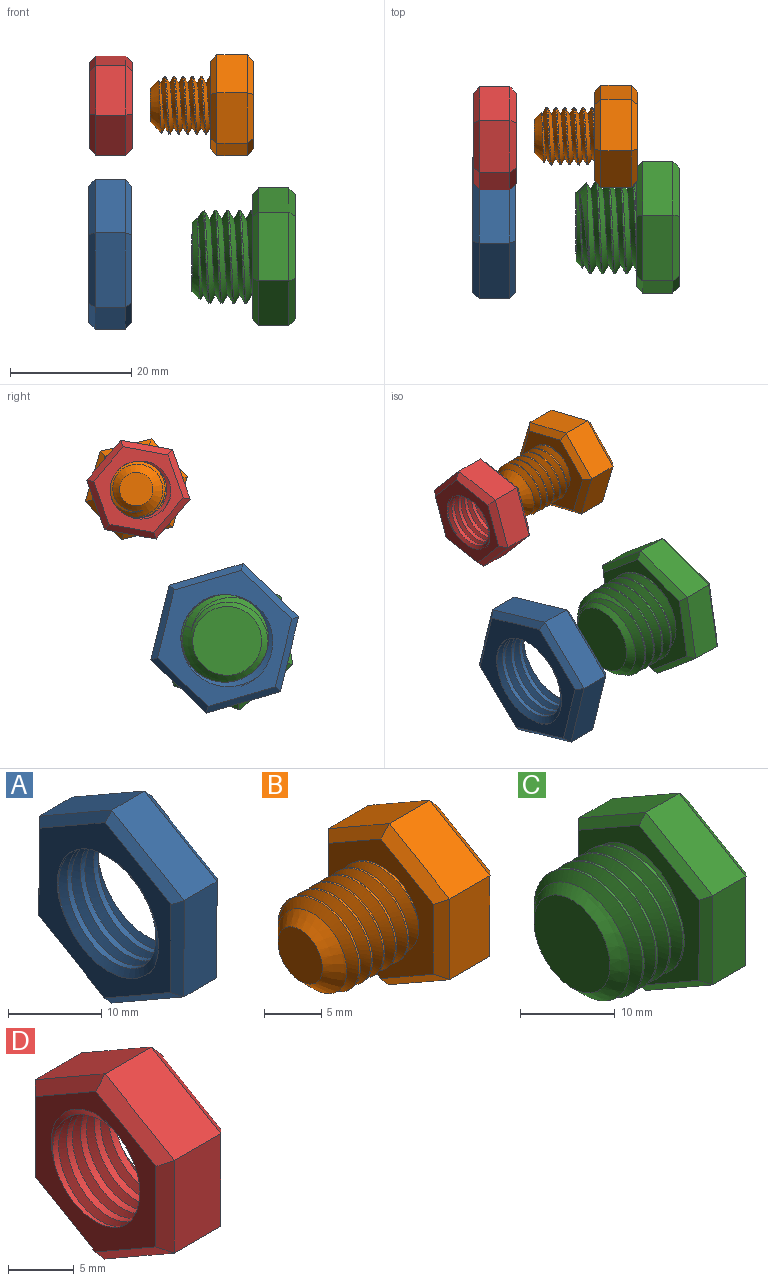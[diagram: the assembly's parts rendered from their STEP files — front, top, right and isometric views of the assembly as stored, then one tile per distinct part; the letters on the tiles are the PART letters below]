
ASSEMBLY  parts=4 mates=2
PART A: 23 faces, bbox 9.3x22.7x26 mm
  f0: cylinder r=7.24mm len=14.48mm, axis (1,0,0), area 111.6mm2, adj f7,f8,f21,f22
  f1: plane 10.98x6.38mm, normal (0,-0.5,0.86), area 63.5mm2, adj f2,f6,f14,f18
  f2: plane 12.7x5mm, normal (0,-1,0), area 63.5mm2, adj f1,f3,f12,f16
  f3: plane 11.02x6.32mm, normal (0,-0.5,-0.87), area 63.5mm2, adj f2,f4,f10,f15
  f4: plane 10.98x6.38mm, normal (0,0.5,-0.86), area 63.5mm2, adj f3,f5,f9,f17
  f5: plane 12.7x5mm, normal (0,1,0), area 63.5mm2, adj f4,f6,f11,f19
  f6: plane 11.02x6.32mm, normal (0,0.5,0.87), area 63.5mm2, adj f1,f5,f13,f20
  f7: plane 23.73x20.67mm, normal (-1,0,0), area 164.4mm2, adj f0,f9,f10,f11,f12,f13,f14,f21
  f8: plane 23.73x20.67mm, normal (1,0,0), area 164.4mm2, adj f0,f15,f16,f17,f18,f19,f20,f21
  f9: plane 10.99x6.96mm, normal (-0.71,0.36,-0.61), area 17.1mm2, adj f4,f7,f10,f11
  f10: plane 11.02x6.9mm, normal (-0.71,-0.35,-0.61), area 17.1mm2, adj f3,f7,f9,f12
  f11: plane 12.7x1.03mm, normal (-0.71,0.71,0), area 17.1mm2, adj f5,f7,f9,f13
  f12: plane 12.7x1.03mm, normal (-0.71,-0.71,0), area 17.1mm2, adj f2,f7,f10,f14
  f13: plane 11.02x6.9mm, normal (-0.71,0.35,0.61), area 17.1mm2, adj f6,f7,f11,f14
  f14: plane 10.99x6.96mm, normal (-0.71,-0.36,0.61), area 17.1mm2, adj f1,f7,f12,f13
  f15: plane 11.02x6.9mm, normal (0.71,-0.35,-0.61), area 17.1mm2, adj f3,f8,f16,f17
  f16: plane 12.7x1.03mm, normal (0.71,-0.71,0), area 17.1mm2, adj f2,f8,f15,f18
  f17: plane 10.99x6.96mm, normal (0.71,0.36,-0.61), area 17.1mm2, adj f4,f8,f15,f19
  f18: plane 10.99x6.96mm, normal (0.71,-0.36,0.61), area 17.1mm2, adj f1,f8,f16,f20
  f19: plane 12.7x1.03mm, normal (0.71,0.71,0), area 17.1mm2, adj f5,f8,f17,f20
  f20: plane 11.02x6.9mm, normal (0.71,0.35,0.61), area 17.1mm2, adj f6,f8,f18,f19
  f21: bspline ~19.31x16.73mm, area 223mm2, adj f0,f7,f8,f22
  f22: bspline ~19.31x16.73mm, area 223mm2, adj f0,f7,f8,f21
PART B: 25 faces, bbox 17.8x15.9x18.1 mm
  f0: cylinder r=4.75mm len=9.5mm, axis (1,0,0), area 28.1mm2, adj f1,f2,f4,f12
  f1: bspline ~10.97x9.91mm, area 196.7mm2, adj f0,f2,f4,f12
  f2: bspline ~10.97x10.66mm, area 196.6mm2, adj f0,f1,f4,f12
  f3: plane 5.5x5.5mm, normal (-1,0,0), area 23.8mm2, adj f4
  f4: cone r=4.75mm half-angle=45deg, axis (1,0,0), area 47.4mm2, adj f0,f1,f2,f3
  f5: plane 7.48x5mm, normal (0,-0.5,0.86), area 43.3mm2, adj f6,f10,f18,f22
  f6: plane 8.66x5mm, normal (0,-1,0), area 43.3mm2, adj f5,f7,f16,f20
  f7: plane 7.52x5mm, normal (0,-0.5,-0.87), area 43.3mm2, adj f6,f8,f14,f19
  f8: plane 7.48x5mm, normal (0,0.5,-0.86), area 43.3mm2, adj f7,f9,f13,f21
  f9: plane 8.66x5mm, normal (0,1,0), area 43.3mm2, adj f8,f10,f15,f23
  f10: plane 7.52x5mm, normal (0,0.5,0.87), area 43.3mm2, adj f5,f9,f17,f24
  f11: plane 15.01x13.03mm, normal (1,0,0), area 146.4mm2, adj f13,f14,f15,f16,f17,f18
  f12: plane 15.83x13.85mm, normal (-1,0,0), area 89.2mm2, adj f0,f1,f2,f19,f20,f21,f22,f23
  f13: plane 7.49x4.93mm, normal (0.71,0.36,-0.61), area 11.4mm2, adj f8,f11,f14,f15
  f14: plane 7.52x4.88mm, normal (0.71,-0.35,-0.61), area 11.4mm2, adj f7,f11,f13,f16
  f15: plane 8.66x1.03mm, normal (0.71,0.71,0), area 11.4mm2, adj f9,f11,f13,f17
  f16: plane 8.66x1.03mm, normal (0.71,-0.71,0), area 11.4mm2, adj f6,f11,f14,f18
  f17: plane 7.52x4.88mm, normal (0.71,0.35,0.61), area 11.4mm2, adj f10,f11,f15,f18
  f18: plane 7.49x4.93mm, normal (0.71,-0.36,0.61), area 11.4mm2, adj f5,f11,f16,f17
  f19: plane 7.52x4.88mm, normal (-0.71,-0.35,-0.61), area 11.4mm2, adj f7,f12,f20,f21
  f20: plane 8.66x1.03mm, normal (-0.71,-0.71,0), area 11.4mm2, adj f6,f12,f19,f22
  f21: plane 7.49x4.93mm, normal (-0.71,0.36,-0.61), area 11.4mm2, adj f8,f12,f19,f23
  f22: plane 7.49x4.93mm, normal (-0.71,-0.36,0.61), area 11.4mm2, adj f5,f12,f20,f24
  f23: plane 8.66x1.03mm, normal (-0.71,0.71,0), area 11.4mm2, adj f9,f12,f21,f24
  f24: plane 7.52x4.88mm, normal (-0.71,0.35,0.61), area 11.4mm2, adj f10,f12,f22,f23
PART C: 26 faces, bbox 17.7x20x23.1 mm
  f0: cylinder r=7.68mm len=15.36mm, axis (1,0,0), area 49.5mm2, adj f1,f2,f5,f13
  f1: bspline ~17.74x15.36mm, area 332.4mm2, adj f0,f2,f4,f5,f13
  f2: bspline ~17.74x15.36mm, area 332.4mm2, adj f0,f1,f4,f5,f13
  f3: plane 11.36x11.36mm, normal (-1,0,0), area 101.4mm2, adj f4
  f4: cone r=7.68mm half-angle=45deg, axis (1,0,0), area 63.2mm2, adj f1,f2,f3,f5
  f5: cone r=7.68mm half-angle=45deg, axis (1,0,0), area 13.2mm2, adj f0,f1,f2,f4
  f6: plane 9.98x5.81mm, normal (0,-0.5,0.86), area 57.7mm2, adj f7,f11,f19,f23
  f7: plane 11.55x5mm, normal (0,-1,0), area 57.7mm2, adj f6,f8,f17,f21
  f8: plane 10.02x5.74mm, normal (0,-0.5,-0.87), area 57.7mm2, adj f7,f9,f15,f20
  f9: plane 9.98x5.81mm, normal (0,0.5,-0.86), area 57.7mm2, adj f8,f10,f14,f22
  f10: plane 11.55x5mm, normal (0,1,0), area 57.7mm2, adj f9,f11,f16,f24
  f11: plane 10.02x5.74mm, normal (0,0.5,0.87), area 57.7mm2, adj f6,f10,f18,f25
  f12: plane 20.78x18.04mm, normal (1,0,0), area 280.6mm2, adj f14,f15,f16,f17,f18,f19
  f13: plane 20.78x18.04mm, normal (-1,0,0), area 125.2mm2, adj f0,f1,f2,f20,f21,f22,f23,f24
  f14: plane 9.98x6.38mm, normal (0.71,0.36,-0.61), area 15.5mm2, adj f9,f12,f15,f16
  f15: plane 10.02x6.32mm, normal (0.71,-0.35,-0.61), area 15.5mm2, adj f8,f12,f14,f17
  f16: plane 11.55x1.04mm, normal (0.71,0.71,0), area 15.5mm2, adj f10,f12,f14,f18
  f17: plane 11.55x1.04mm, normal (0.71,-0.71,0), area 15.5mm2, adj f7,f12,f15,f19
  f18: plane 10.02x6.32mm, normal (0.71,0.35,0.61), area 15.5mm2, adj f11,f12,f16,f19
  f19: plane 9.98x6.38mm, normal (0.71,-0.36,0.61), area 15.5mm2, adj f6,f12,f17,f18
  f20: plane 10.02x6.32mm, normal (-0.71,-0.35,-0.61), area 15.5mm2, adj f8,f13,f21,f22
  f21: plane 11.55x1.04mm, normal (-0.71,-0.71,0), area 15.5mm2, adj f7,f13,f20,f23
  f22: plane 9.98x6.38mm, normal (-0.71,0.36,-0.61), area 15.5mm2, adj f9,f13,f20,f24
  f23: plane 9.98x6.38mm, normal (-0.71,-0.36,0.61), area 15.5mm2, adj f6,f13,f21,f25
  f24: plane 11.55x1.04mm, normal (-0.71,0.71,0), area 15.5mm2, adj f10,f13,f22,f25
  f25: plane 10.02x6.32mm, normal (-0.71,0.35,0.61), area 15.5mm2, adj f11,f13,f23,f24
PART D: 23 faces, bbox 9.1x15.4x17.7 mm
  f0: plane 7.49x5mm, normal (0,-0.5,0.86), area 43.3mm2, adj f1,f5,f13,f17
  f1: plane 8.66x5mm, normal (0,-1,0), area 43.3mm2, adj f0,f2,f11,f15
  f2: plane 7.51x5mm, normal (0,-0.5,-0.87), area 43.3mm2, adj f1,f3,f9,f14
  f3: plane 7.49x5mm, normal (0,0.5,-0.86), area 43.3mm2, adj f2,f4,f8,f16
  f4: plane 8.66x5mm, normal (0,1,0), area 43.3mm2, adj f3,f5,f10,f18
  f5: plane 7.51x5mm, normal (0,0.5,0.87), area 43.3mm2, adj f0,f4,f12,f19
  f6: plane 15.37x13.38mm, normal (-1,0,0), area 71.4mm2, adj f8,f9,f10,f11,f12,f13,f20,f21
  f7: plane 15.37x13.38mm, normal (1,0,0), area 71.4mm2, adj f14,f15,f16,f17,f18,f19,f20,f21
  f8: plane 7.49x4.93mm, normal (-0.71,0.36,-0.61), area 11.4mm2, adj f3,f6,f9,f10
  f9: plane 7.51x4.89mm, normal (-0.71,-0.35,-0.61), area 11.4mm2, adj f2,f6,f8,f11
  f10: plane 8.66x1.02mm, normal (-0.71,0.71,0), area 11.4mm2, adj f4,f6,f8,f12
  f11: plane 8.66x1.02mm, normal (-0.71,-0.71,0), area 11.4mm2, adj f1,f6,f9,f13
  f12: plane 7.51x4.89mm, normal (-0.71,0.35,0.61), area 11.4mm2, adj f5,f6,f10,f13
  f13: plane 7.49x4.93mm, normal (-0.71,-0.36,0.61), area 11.4mm2, adj f0,f6,f11,f12
  f14: plane 7.51x4.89mm, normal (0.71,-0.35,-0.61), area 11.4mm2, adj f2,f7,f15,f16
  f15: plane 8.66x1.02mm, normal (0.71,-0.71,0), area 11.4mm2, adj f1,f7,f14,f17
  f16: plane 7.49x4.93mm, normal (0.71,0.36,-0.61), area 11.4mm2, adj f3,f7,f14,f18
  f17: plane 7.49x4.93mm, normal (0.71,-0.36,0.61), area 11.4mm2, adj f0,f7,f15,f19
  f18: plane 8.66x1.02mm, normal (0.71,0.71,0), area 11.4mm2, adj f4,f7,f16,f19
  f19: plane 7.51x4.89mm, normal (0.71,0.35,0.61), area 11.4mm2, adj f5,f7,f17,f18
  f20: cylinder r=4.66mm len=9.32mm, axis (1,0,0), area 85.4mm2, adj f6,f7,f21,f22
  f21: bspline ~12.5x10.82mm, area 128.4mm2, adj f6,f7,f20,f22
  f22: bspline ~12.5x10.82mm, area 128.5mm2, adj f6,f7,f20,f21
PLACE A rot(axis=(0,0.6,-0.8),180deg) t=(-55.27,-6.86,23.48)mm fixed
PLACE B rot(axis=(-1,0,0),43.8deg) t=(-31.66,7.73,48.08)mm
PLACE C rot(axis=(1,0,0),109.9deg) t=(-24.77,-7.25,23.06)mm
PLACE D rot(axis=(1,0,0),100.2deg) t=(-48.16,7.38,48.02)mm fixed
MATE cylindrical C.f0 <-> A.f7  axis (-1,0,0) through (-38.27,-7.25,23.06)mm
MATE cylindrical B.f0 <-> D.f6  axis (-1,0,0) through (-45.16,7.73,48.08)mm
